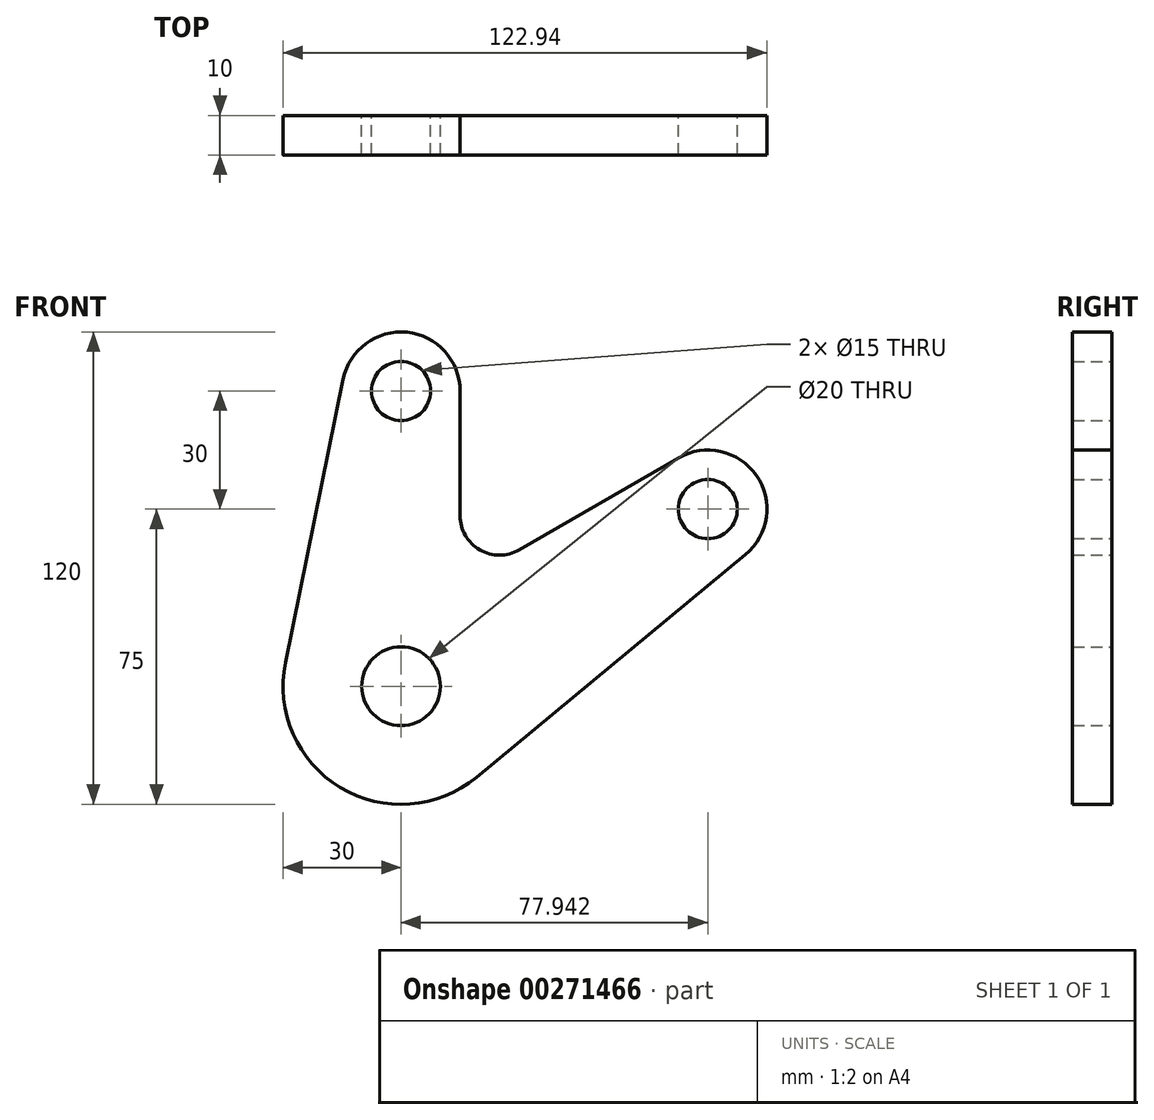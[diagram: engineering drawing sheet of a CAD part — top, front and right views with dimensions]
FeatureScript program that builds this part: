
annotation { "Feature Type Name" : "Feature", "Feature Type Description" : "" }
export const myFeature = defineFeature(function(context is Context, id is Id, definition is map)
    precondition{}
    {
        {
            var Q0;
            Q0=qCreatedBy(makeId("Front.planeOp"),FACE);
            var sketch = newSketch(context, id + "F0", { "sketchPlane" : qUnion([Q0])});
            skCircle(sketch, "E0", {"center": v(0, 0) * mm, "radius": 10 * mm});
            skCircle(sketch, "E1", {"center": v(0, 75) * mm, "radius": 7.5 * mm});
            skCircle(sketch, "E2", {"center": v(77.94, 45) * mm, "radius": 7.5 * mm});
            skLineSegment(sketch, "E3", {"start": v(-14.7, 78) * mm, "end": v(-29.4, 6) * mm});
            skLineSegment(sketch, "E4", {"start": v(15, 75) * mm, "end": v(15, 43.3) * mm});
            skLineSegment(sketch, "E5", {"start": v(70.44, 58) * mm, "end": v(30, 34.64) * mm});
            skLineSegment(sketch, "E6", {"start": v(87.5, 33.44) * mm, "end": v(19.12, -23.12) * mm});
            skArc(sketch, "E7", {"start": v(15, 43.3) * mm, "mid": v(20, 34.64) * mm, "end": v(30, 34.64) * mm});
            skArc(sketch, "E8", {"start": v(-14.7, 78) * mm, "mid": v(1.5, 89.92) * mm, "end": v(15, 75) * mm});
            skArc(sketch, "E9", {"start": v(-29.4, 6) * mm, "mid": v(-15.44, -25.72) * mm, "end": v(19.12, -23.12) * mm});
            skArc(sketch, "E10", {"start": v(87.5, 33.44) * mm, "mid": v(90.26, 53.56) * mm, "end": v(70.44, 58) * mm});
            skLineSegment(sketch, "E11", {"start": v(77.94, 45) * mm, "end": v(0, 0) * mm, "construction": true});
            skLineSegment(sketch, "E12", {"start": v(0, 75) * mm, "end": v(0, 0) * mm, "construction": true});
            skSolve(sketch);
        }
        {
            var Q0;
            Q0 = qSketchRegion(id + "F0", true);
            extrude(context, id + "F1", {"entities" : qUnion([Q0]), "depth" : 10 * mm});
        }
    });
